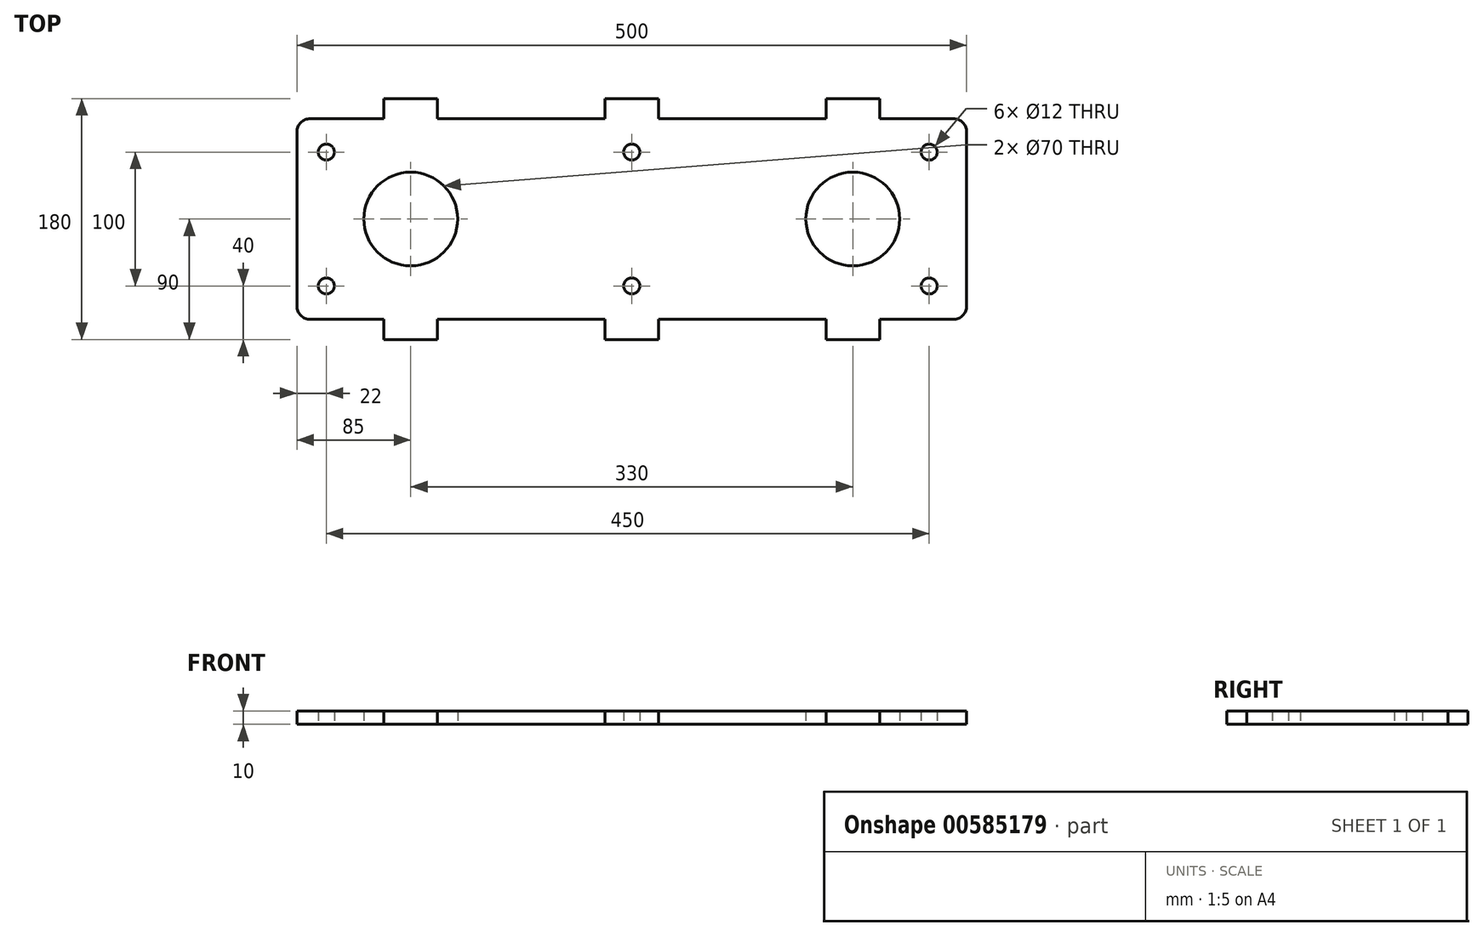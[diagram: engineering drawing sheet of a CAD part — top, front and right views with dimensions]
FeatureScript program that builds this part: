
annotation { "Feature Type Name" : "Feature", "Feature Type Description" : "" }
export const myFeature = defineFeature(function(context is Context, id is Id, definition is map)
    precondition{}
    {
        {
            var Q0;
            Q0=qCreatedBy(makeId("Top.planeOp"),FACE);
            var sketch = newSketch(context, id + "F0", { "sketchPlane" : qUnion([Q0])});
            skLineSegment(sketch, "E0.bottom", {"start": v(10, 0) * mm, "end": v(490, 0) * mm});
            skLineSegment(sketch, "E0.top", {"start": v(10, 150) * mm, "end": v(490, 150) * mm});
            skLineSegment(sketch, "E0.left", {"start": v(0, 10) * mm, "end": v(0, 140) * mm});
            skLineSegment(sketch, "E0.right", {"start": v(500, 10) * mm, "end": v(500, 140) * mm});
            skPoint(sketch, "E1.visualSharp", {"position": v(0, 150) * mm});
            skArc(sketch, "E1.filletArc", {"start": v(10, 150) * mm, "mid": v(2.93, 147.07) * mm, "end": v(0, 140) * mm});
            skPoint(sketch, "E2.visualSharp", {"position": v(500, 150) * mm});
            skArc(sketch, "E2.filletArc", {"start": v(500, 140) * mm, "mid": v(497.07, 147.07) * mm, "end": v(490, 150) * mm});
            skPoint(sketch, "E3.visualSharp", {"position": v(500, 0) * mm});
            skArc(sketch, "E3.filletArc", {"start": v(490, 0) * mm, "mid": v(497.07, 2.93) * mm, "end": v(500, 10) * mm});
            skPoint(sketch, "E4.visualSharp", {"position": v(0, 0) * mm});
            skArc(sketch, "E4.filletArc", {"start": v(0, 10) * mm, "mid": v(2.93, 2.93) * mm, "end": v(10, 0) * mm});
            skCircle(sketch, "E5", {"center": v(85, 75) * mm, "radius": 35 * mm});
            skCircle(sketch, "E6", {"center": v(415, 75) * mm, "radius": 35 * mm});
            skCircle(sketch, "E7", {"center": v(22, 125) * mm, "radius": 6 * mm});
            skCircle(sketch, "E8", {"center": v(472, 125) * mm, "radius": 6 * mm});
            skCircle(sketch, "E9", {"center": v(250, 125) * mm, "radius": 6 * mm});
            skCircle(sketch, "E10", {"center": v(472, 25) * mm, "radius": 6 * mm});
            skCircle(sketch, "E11", {"center": v(250, 25) * mm, "radius": 6 * mm});
            skCircle(sketch, "E12", {"center": v(22, 25) * mm, "radius": 6 * mm});
            skLineSegment(sketch, "E13.bottom", {"start": v(65, 0) * mm, "end": v(105, 0) * mm});
            skLineSegment(sketch, "E13.top", {"start": v(65, -15) * mm, "end": v(105, -15) * mm});
            skLineSegment(sketch, "E13.left", {"start": v(65, 0) * mm, "end": v(65, -15) * mm});
            skLineSegment(sketch, "E13.right", {"start": v(105, 0) * mm, "end": v(105, -15) * mm});
            skLineSegment(sketch, "E14.bottom", {"start": v(230, 0) * mm, "end": v(270, 0) * mm});
            skLineSegment(sketch, "E14.top", {"start": v(230, -15) * mm, "end": v(270, -15) * mm});
            skLineSegment(sketch, "E14.left", {"start": v(230, 0) * mm, "end": v(230, -15) * mm});
            skLineSegment(sketch, "E14.right", {"start": v(270, 0) * mm, "end": v(270, -15) * mm});
            skLineSegment(sketch, "E15.bottom", {"start": v(395, 0) * mm, "end": v(435, 0) * mm});
            skLineSegment(sketch, "E15.top", {"start": v(395, -15) * mm, "end": v(435, -15) * mm});
            skLineSegment(sketch, "E15.left", {"start": v(395, 0) * mm, "end": v(395, -15) * mm});
            skLineSegment(sketch, "E15.right", {"start": v(435, 0) * mm, "end": v(435, -15) * mm});
            skLineSegment(sketch, "E16.bottom", {"start": v(65, 150) * mm, "end": v(105, 150) * mm});
            skLineSegment(sketch, "E16.top", {"start": v(65, 165) * mm, "end": v(105, 165) * mm});
            skLineSegment(sketch, "E16.left", {"start": v(65, 150) * mm, "end": v(65, 165) * mm});
            skLineSegment(sketch, "E16.right", {"start": v(105, 150) * mm, "end": v(105, 165) * mm});
            skLineSegment(sketch, "E17.bottom", {"start": v(230, 150) * mm, "end": v(270, 150) * mm});
            skLineSegment(sketch, "E17.top", {"start": v(230, 165) * mm, "end": v(270, 165) * mm});
            skLineSegment(sketch, "E17.left", {"start": v(230, 150) * mm, "end": v(230, 165) * mm});
            skLineSegment(sketch, "E17.right", {"start": v(270, 150) * mm, "end": v(270, 165) * mm});
            skLineSegment(sketch, "E18.bottom", {"start": v(395, 150) * mm, "end": v(435, 150) * mm});
            skLineSegment(sketch, "E18.top", {"start": v(395, 165) * mm, "end": v(435, 165) * mm});
            skLineSegment(sketch, "E18.left", {"start": v(395, 150) * mm, "end": v(395, 165) * mm});
            skLineSegment(sketch, "E18.right", {"start": v(435, 150) * mm, "end": v(435, 165) * mm});
            skPoint(sketch, "E19", {"position": v(85, -15) * mm});
            skPoint(sketch, "E20", {"position": v(250, -15) * mm});
            skPoint(sketch, "E21", {"position": v(415, -15) * mm});
            skSolve(sketch);
        }
        {
            var Q0;
            Q0 = qSketchRegion(id + "F0", true);
            extrude(context, id + "F1", {"entities" : qUnion([Q0]), "depth" : 10 * mm, "offsetDistance" : 25 * mm});
        }
    });
